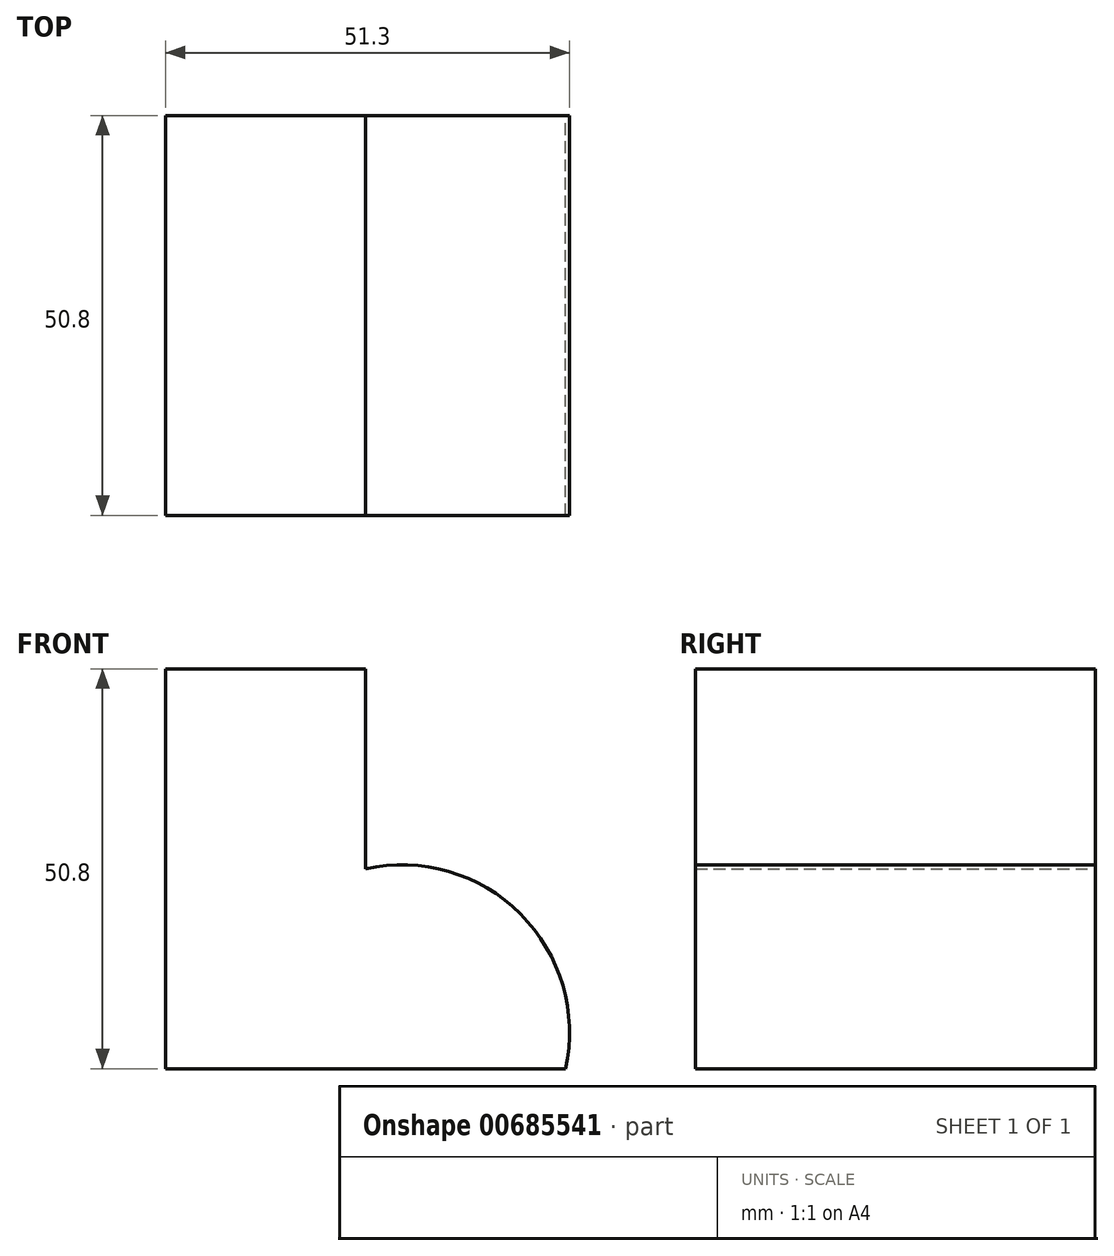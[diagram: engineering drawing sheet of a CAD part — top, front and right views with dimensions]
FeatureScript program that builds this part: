
annotation { "Feature Type Name" : "Feature", "Feature Type Description" : "" }
export const myFeature = defineFeature(function(context is Context, id is Id, definition is map)
    precondition{}
    {
        {
            var Q0;
            Q0=qCreatedBy(makeId("Front.planeOp"),FACE);
            var sketch = newSketch(context, id + "F0", { "sketchPlane" : qUnion([Q0])});
            skLineSegment(sketch, "E0", {"start": v(0, 0) * mm, "end": v(-50.8, 0) * mm});
            skLineSegment(sketch, "E1", {"start": v(-50.8, 0) * mm, "end": v(-50.8, 50.8) * mm});
            skLineSegment(sketch, "E2", {"start": v(-50.8, 50.8) * mm, "end": v(-25.4, 50.8) * mm});
            skLineSegment(sketch, "E3", {"start": v(-25.4, 50.8) * mm, "end": v(-25.4, 25.4) * mm});
            skArc(sketch, "E4", {"start": v(0, 0) * mm, "mid": v(-5.74, 19.66) * mm, "end": v(-25.4, 25.4) * mm});
            skSolve(sketch);
        }
        {
            var Q0;
            Q0=makeQuery(id+"F0.imprint","IMPRINT",FACE,{"disambiguationData":[TD([[makeQuery(id+"F0.imprint","IMPRINT",EDGE,{"derivedFrom":sQuery(id+"F0.wireOp",EDGE,"E0")}),-1.0]])]});
            extrude(context, id + "F1", {"entities" : qUnion([Q0]), "depth" : 50.8 * mm, "offsetDistance" : 25.4 * mm});
        }
    });
